# Revit family: Плиты опорные ПО
name_source: partatom
category: Обобщенные модели
units: mm (PartAtom-declared; Revit-internal decimal feet)

## family parameters
Всегда вертикально = Да
Может служить основой для арматурных стержней = Нет
На основе рабочей плоскости = Нет
Общий = Нет
При загрузке вырезать с полостями = Нет
Размер круглого соединителя = Использовать диаметр
Тип детали = Нормальный
Точка расчета площади = Нет

## types (4) — shared parameters
ADSK_Изготовитель = АО СВЯЗЬСТРОЙДЕТАЛЬ
ADSK_Класс бетона = В15
ADSK_Сертификат соответствия = https://www.ssd.ru
ADSK_Ссылка на сайт = https://www.ssd.ru

## per-type parameters (varying)
| type | ADSK_Высота | ADSK_Код изделия | ADSK_Марка | ADSK_Масса |
| Плита опорная ПО-2 под колодец ККСр-2 | 100 мм | 110402-00089 | ПО-2 | 411 |
| Плита опорная ПО-3 под колодец ККСр-3 | 100 мм | 110402-00078 | ПО-3 | 582 |
| Плита опорная ПО-4 под колодец ККСр-4 | 120 мм | 110402-00090 | ПО-4 | 1050 |
| Плита опорная ПО-5 под колодец ККСр-5 | 130 мм | 110402-00091 | ПО-5 | 1700 |

note: column(s) folded — value = type name in every type: ADSK_Наименование
